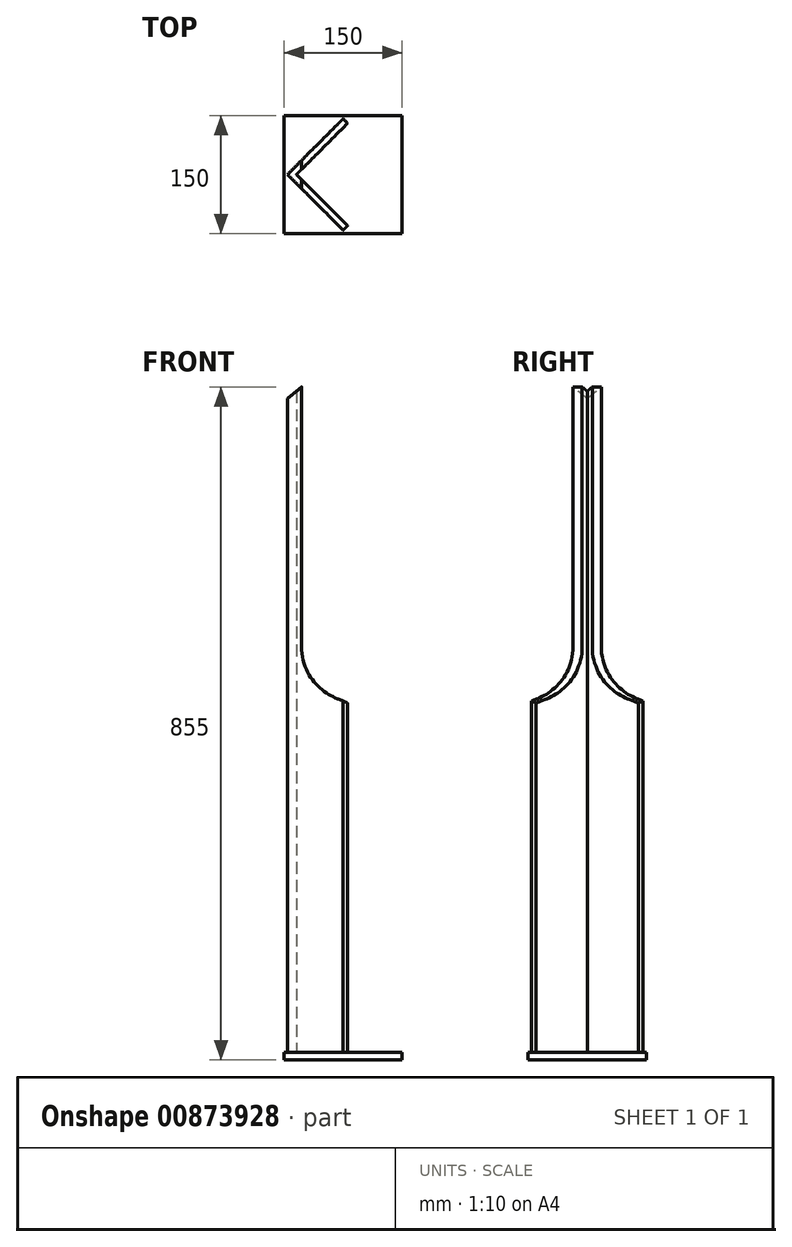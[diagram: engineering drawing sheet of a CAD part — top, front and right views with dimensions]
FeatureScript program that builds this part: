
annotation { "Feature Type Name" : "Feature", "Feature Type Description" : "" }
export const myFeature = defineFeature(function(context is Context, id is Id, definition is map)
    precondition{}
    {
        {
            var Q0;
            Q0=qCreatedBy(makeId("Front.planeOp"),FACE);
            var sketch = newSketch(context, id + "F0", { "sketchPlane" : qUnion([Q0])});
            skLineSegment(sketch, "E0", {"start": v(0, 0) * mm, "end": v(-800, 0) * mm, "construction": true});
            skLineSegment(sketch, "E1.right", {"start": v(-800, 165) * mm, "end": v(-800, -165) * mm, "construction": true});
            skArc(sketch, "E2", {"start": v(-800, -165) * mm, "mid": v(-790.22, -197.83) * mm, "end": v(-764.08, -219.96) * mm, "construction": true});
            skLineSegment(sketch, "E3", {"start": v(-800, -165) * mm, "end": v(0, -165) * mm, "construction": true});
            skLineSegment(sketch, "E4", {"start": v(0, -165) * mm, "end": v(0, 0) * mm, "construction": true});
            skLineSegment(sketch, "E5", {"start": v(0, -165) * mm, "end": v(0, -380) * mm, "construction": true});
            skArc(sketch, "E6", {"start": v(-764.08, -219.96) * mm, "mid": v(-390.33, -339.56) * mm, "end": v(0, -380) * mm, "construction": true});
            skArc(sketch, "E7.0", {"start": v(-766.49, -225.45) * mm, "mid": v(-391.56, -345.43) * mm, "end": v(0, -386) * mm});
            skArc(sketch, "E7.1", {"start": v(-806, -165) * mm, "mid": v(-795.25, -201.11) * mm, "end": v(-766.49, -225.45) * mm});
            skLineSegment(sketch, "E7.2", {"start": v(-806, 165) * mm, "end": v(-806, -165) * mm});
            skArc(sketch, "E8.0", {"start": v(-768.9, -230.95) * mm, "mid": v(-392.8, -351.3) * mm, "end": v(0, -392) * mm});
            skArc(sketch, "E8.1", {"start": v(-812, -165) * mm, "mid": v(-800.27, -204.4) * mm, "end": v(-768.9, -230.95) * mm});
            skLineSegment(sketch, "E8.2", {"start": v(-812, 165) * mm, "end": v(-812, -165) * mm});
            skLineSegment(sketch, "E9", {"start": v(-800, 165) * mm, "end": v(-759, 165) * mm, "construction": true});
            skLineSegment(sketch, "E10", {"start": v(-759, 165) * mm, "end": v(-759, -228.71) * mm, "construction": true});
            skLineSegment(sketch, "E11", {"start": v(-759, 165) * mm, "end": v(-759, -235.25) * mm});
            skLineSegment(sketch, "E12", {"start": v(-812, 165) * mm, "end": v(-806, 165) * mm});
            skLineSegment(sketch, "E13", {"start": v(-806, 165) * mm, "end": v(-759, 165) * mm});
            skLineSegment(sketch, "E14.top", {"start": v(-759, 165) * mm, "end": v(-709.97, 165) * mm});
            skLineSegment(sketch, "E14.left", {"start": v(-759, -235.25) * mm, "end": v(-759, 165) * mm});
            skLineSegment(sketch, "E14.right", {"start": v(-709.97, -235.25) * mm, "end": v(-709.97, 165) * mm});
            skLineSegment(sketch, "E15", {"start": v(-709.97, -235.25) * mm, "end": v(-709.97, -255.6) * mm});
            skLineSegment(sketch, "E16", {"start": v(-812, 165) * mm, "end": v(-842, 165) * mm});
            skLineSegment(sketch, "E17", {"start": v(-842, 165) * mm, "end": v(-842, 140) * mm});
            skLineSegment(sketch, "E18", {"start": v(-842, 140) * mm, "end": v(-812, 165) * mm});
            skSolve(sketch);
        }
        {
            var Q0;
            {var subQ4=sQuery(id+"F0.wireOp",EDGE,"E7.1");Q0=makeQuery(id+"F0.imprint","IMPRINT",FACE,{"disambiguationData":[TD([[makeQuery(id+"F0.imprint","IMPRINT",EDGE,{"derivedFrom":subQ4}),-1.0]])]});}
            var Q1;
            Q1=sQuery(id+"F0.wireOp",EDGE,"E4");
            revolve(context, id + "F1", {"surfaceOperationType" : NewSurfaceOperationType.NEW, "entities" : qUnion([Q0]), "axis" : qUnion([Q1]), "revolveType" : RevolveType.SYMMETRIC, "angle" : 30 * degree});
        }
        {
            var Q0;
            Q0=qCreatedBy(makeId("Right.planeOp"),FACE);
            var sketch = newSketch(context, id + "F2", { "sketchPlane" : qUnion([Q0])});
            skLineSegment(sketch, "E19.bottom", {"start": v(85, 165) * mm, "end": v(-85, 165) * mm});
            skLineSegment(sketch, "E19.top", {"start": v(85, -240) * mm, "end": v(-85, -240) * mm});
            skLineSegment(sketch, "E19.left", {"start": v(85, 165) * mm, "end": v(85, -240) * mm});
            skLineSegment(sketch, "E19.right", {"start": v(-85, 165) * mm, "end": v(-85, -240) * mm});
            skLineSegment(sketch, "E20", {"start": v(0, 165) * mm, "end": v(0, -165) * mm, "construction": true});
            skLineSegment(sketch, "E21.bottom", {"start": v(305.39, 374.4) * mm, "end": v(-305.39, 374.4) * mm});
            skLineSegment(sketch, "E21.top", {"start": v(305.39, -374.4) * mm, "end": v(-305.39, -374.4) * mm});
            skLineSegment(sketch, "E21.left", {"start": v(305.39, 374.4) * mm, "end": v(305.39, -374.4) * mm});
            skLineSegment(sketch, "E21.right", {"start": v(-305.39, 374.4) * mm, "end": v(-305.39, -374.4) * mm});
            skPoint(sketch, "E21.middle", {"position": v(0, 0) * mm});
            skSolve(sketch);
        }
        {
            var Q0;
            Q0=makeQuery(id+"F2.imprint","IMPRINT",FACE,{"disambiguationData":[TD([[makeQuery(id+"F2.imprint","IMPRINT",EDGE,{"derivedFrom":sQuery(id+"F2.wireOp",EDGE,"E19.bottom")}),-1.0]])]});
            extrude(context, id + "F3", {"entities" : qUnion([Q0]), "operationType" : NewBodyOperationType.REMOVE, "endBound" : BoundingType.THROUGH_ALL, "oppositeDirection" : true, "depth" : 25 * mm, "offsetDistance" : 25 * mm});
        }
        {
            var Q0;
            Q0=qCreatedBy(makeId("Top.planeOp"),FACE);
            cPlane(context, id + "F4", {"entities" : qUnion([Q0]), "cplaneType" : CPlaneType.OFFSET, "offset" : 680 * mm, "oppositeDirection" : true, "width" : 150 * mm, "height" : 150 * mm});
        }
        {
            var Q0;
            Q0=qCreatedBy(id+"F4.planeOp",FACE);
            var sketch = newSketch(context, id + "F5", { "sketchPlane" : qUnion([Q0])});
            skLineSegment(sketch, "E22", {"start": v(0, 0) * mm, "end": v(-759, 0) * mm, "construction": true});
            skLineSegment(sketch, "E23.bottom", {"start": v(-834, 75) * mm, "end": v(-684, 75) * mm});
            skLineSegment(sketch, "E23.top", {"start": v(-834, -75) * mm, "end": v(-684, -75) * mm});
            skLineSegment(sketch, "E23.left", {"start": v(-834, 75) * mm, "end": v(-834, -75) * mm});
            skLineSegment(sketch, "E23.right", {"start": v(-684, 75) * mm, "end": v(-684, -75) * mm});
            skPoint(sketch, "E23.middle", {"position": v(-759, 0) * mm});
            skLineSegment(sketch, "E24", {"start": v(-1100.35, 0) * mm, "end": v(-829.71, 0) * mm, "construction": true});
            skLineSegment(sketch, "E25", {"start": v(-829.71, 0) * mm, "end": v(-759, -70.71) * mm});
            skLineSegment(sketch, "E26.MirrorCS", {"start": v(-829.71, 0) * mm, "end": v(-759, 70.71) * mm});
            skLineSegment(sketch, "E27.0", {"start": v(-818.4, 0) * mm, "end": v(-753.34, 65.05) * mm});
            skLineSegment(sketch, "E27.1", {"start": v(-818.4, 0) * mm, "end": v(-753.34, -65.05) * mm});
            skLineSegment(sketch, "E28", {"start": v(-759, 70.71) * mm, "end": v(-753.34, 65.05) * mm});
            skLineSegment(sketch, "E29", {"start": v(-753.34, -65.05) * mm, "end": v(-759, -70.71) * mm});
            skLineSegment(sketch, "E30", {"start": v(-759, 70.71) * mm, "end": v(-759, -70.71) * mm, "construction": true});
            skSolve(sketch);
        }
        {
            var Q0;
            Q0=makeQuery(id+"F5.imprint","IMPRINT",FACE,{"disambiguationData":[TD([[makeQuery(id+"F5.imprint","IMPRINT",EDGE,{"derivedFrom":sQuery(id+"F5.wireOp",EDGE,"E25")}),1.0]])]});
            extrude(context, id + "F6", {"entities" : qUnion([Q0]), "depth" : 845 * mm, "offsetDistance" : 25 * mm});
        }
        {
            var Q0;
            Q0 = qSketchRegion(id + "F5", true);
            var Q1;
            Q1=makeQuery(id+"F5.imprint","IMPRINT",FACE,{"disambiguationData":[TD([[makeQuery(id+"F5.imprint","IMPRINT",EDGE,{"derivedFrom":sQuery(id+"F5.wireOp",EDGE,"E25")}),1.0]])]});
            extrude(context, id + "F7", {"entities" : qUnion([Q0, Q1]), "oppositeDirection" : true, "depth" : 10 * mm, "offsetDistance" : 25 * mm});
        }
        {
            var Q0;
            {var subQ4=sQuery(id+"F0.wireOp",EDGE,"E7.1");Q0=makeQuery(id+"F0.imprint","IMPRINT",FACE,{"disambiguationData":[TD([[makeQuery(id+"F0.imprint","IMPRINT",EDGE,{"derivedFrom":subQ4}),1.0]])]});}
            var Q1;
            {var subQ4=sQuery(id+"F0.wireOp",EDGE,"E7.1");Q1=makeQuery(id+"F0.imprint","IMPRINT",FACE,{"disambiguationData":[TD([[makeQuery(id+"F0.imprint","IMPRINT",EDGE,{"derivedFrom":subQ4}),-1.0]])]});}
            var Q2;
            {var subQ1=sQuery(id+"F0.wireOp",EDGE,"E14.top");Q2=makeQuery(id+"F0.imprint","IMPRINT",FACE,{"disambiguationData":[TD([[makeQuery(id+"F0.imprint","IMPRINT",EDGE,{"derivedFrom":subQ1}),-1.0]])]});}
            var Q3;
            {var subQ0=sQuery(id+"F0.wireOp",EDGE,"E15");var subQ1=sQuery(id+"F0.wireOp",EDGE,"E7.0");var subQ2=makeQuery(id+"F0.imprint","INTERSECT",VERTEX,{"derivedFrom":[subQ1,subQ0]});Q3=makeQuery(id+"F0.imprint","IMPRINT",FACE,{"disambiguationData":[TD([[makeQuery(id+"F0.imprint","IMPRINT",EDGE,{"disambiguationData":[TD([[subQ2,1.0]])],"derivedFrom":subQ1}),-1.0]])]});}
            var Q4;
            Q4=sQuery(id+"F0.wireOp",EDGE,"E5");
            revolve(context, id + "F8", {"operationType" : NewBodyOperationType.REMOVE, "surfaceOperationType" : NewSurfaceOperationType.NEW, "entities" : qUnion([Q0, Q1, Q2, Q3]), "axis" : qUnion([Q4]), "revolveType" : RevolveType.FULL, "oppositeDirection" : true});
        }
        {
            var Q0;
            Q0=makeQuery(id+"F0.imprint","IMPRINT",FACE,{"disambiguationData":[TD([[makeQuery(id+"F0.imprint","IMPRINT",EDGE,{"derivedFrom":sQuery(id+"F0.wireOp",EDGE,"E16")}),1.0]])]});
            var Q1;
            Q1=sQuery(id+"F0.wireOp",EDGE,"E5");
            revolve(context, id + "F9", {"operationType" : NewBodyOperationType.REMOVE, "surfaceOperationType" : NewSurfaceOperationType.NEW, "entities" : qUnion([Q0]), "axis" : qUnion([Q1]), "revolveType" : RevolveType.FULL, "oppositeDirection" : true});
        }
    });
